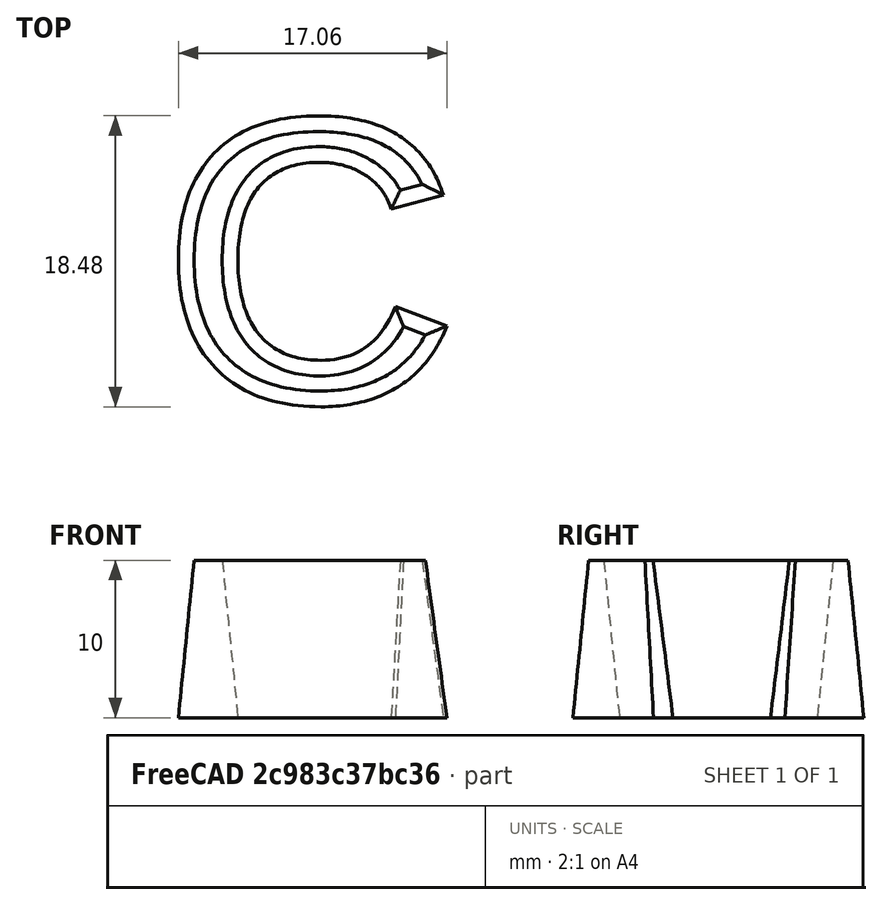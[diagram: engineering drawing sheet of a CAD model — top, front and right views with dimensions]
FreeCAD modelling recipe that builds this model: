
FCSTD DOCUMENT  (FreeCAD 0.21RUnknown)
Label: chars-youtube-mangojelly
License: All rights reserved
LicenseURL: https://en.wikipedia.org/wiki/All_rights_reserved
objects: Part::FeaturePython×4, Part::Part2DObjectPython×2, Part::Extrusion×2, Part::Chamfer×2, Part::Loft×2
note: 12 computed .brp shape members not serialized (recipe doc carries the construction recipe); baked Part::Feature solids carry a one-line shape summary decoded from their .brp

FEATURE [Part::Part2DObjectPython] ShapeString  # Draft 2D object (typed FeaturePython)
  FontFile = /nix/var/nix/profiles/system/sw/share/X11/fonts/LiberationSans-Bold.ttf
  MakeFace = true
  Size = 20
  String = C
  Tracking = 0
FEATURE [Part::Extrusion] Extrude
  Base = -> ShapeString
  Dir = (0,0,1)
  DirMode = 2
  FaceMakerClass = Part::FaceMakerBullseye
  LengthFwd = 10
  LengthRev = 0
  Solid = false
  Symmetric = false
FEATURE [Part::Chamfer] Chamfer
  Base = -> Extrude
  Edges = 17 edges r=1: [Edge4,Edge7,Edge10,Edge13,Edge16,Edge19,Edge22,Edge25,Edge28,Edge31,Edge34,Edge37,Edge40,Edge43,Edge46,Edge49,Edge51]
FEATURE [Part::FeaturePython] Facebinder  # WARN: FeaturePython — macro-defined, semantics opaque (R4)
  Area = 51.5442
  Extrusion = 0
  Faces = -> [Chamfer]
  RemoveSplitter = false
  Sew = false
FEATURE [Part::FeaturePython] Facebinder001  # WARN: FeaturePython — macro-defined, semantics opaque (R4)
  Area = 134.848
  Extrusion = 0
  Faces = -> [Chamfer]
  RemoveSplitter = false
  Sew = false
FEATURE [Part::Loft] Loft
  Closed = false
  MaxDegree = 5
  Ruled = false
  Sections = -> [Facebinder,Facebinder001]
  Solid = true
FEATURE [Part::Part2DObjectPython] ShapeString001  # Draft 2D object (typed FeaturePython)
  FontFile = /nix/var/nix/profiles/system/sw/share/X11/fonts/DejaVuSans-Bold.ttf
  MakeFace = true
  Placement = pos=(20.08,0,0) rot=(0,0,1;0rad)
  Size = 20
  String = D
  Tracking = 0
FEATURE [Part::Extrusion] Extrude001
  Base = -> ShapeString001
  Dir = (0,0,1)
  DirMode = 2
  FaceMakerClass = Part::FaceMakerBullseye
  LengthFwd = 5
  LengthRev = 0
  Solid = false
  Symmetric = false
FEATURE [Part::Chamfer] Chamfer001
  Base = -> Extrude001
  Edges = 18 edges r=1: [Edge4,Edge7,Edge10,Edge13,Edge16,Edge19,Edge22,Edge25,Edge28,Edge31,Edge33,Edge37,Edge40,Edge43,Edge46,Edge49,Edge52,Edge54]
FEATURE [Part::FeaturePython] Facebinder002  # WARN: FeaturePython — macro-defined, semantics opaque (R4)
  Area = 118.461
  Extrusion = 0
  Faces = -> [Chamfer001]
  RemoveSplitter = false
  Sew = false
FEATURE [Part::FeaturePython] Facebinder003  # WARN: FeaturePython — macro-defined, semantics opaque (R4)
  Area = 217.593
  Extrusion = 0
  Faces = -> [Chamfer001]
  RemoveSplitter = false
  Sew = false
FEATURE [Part::Loft] Loft001
  Closed = false
  MaxDegree = 5
  Ruled = false
  Sections = -> [Facebinder002,Facebinder003]
  Solid = false
